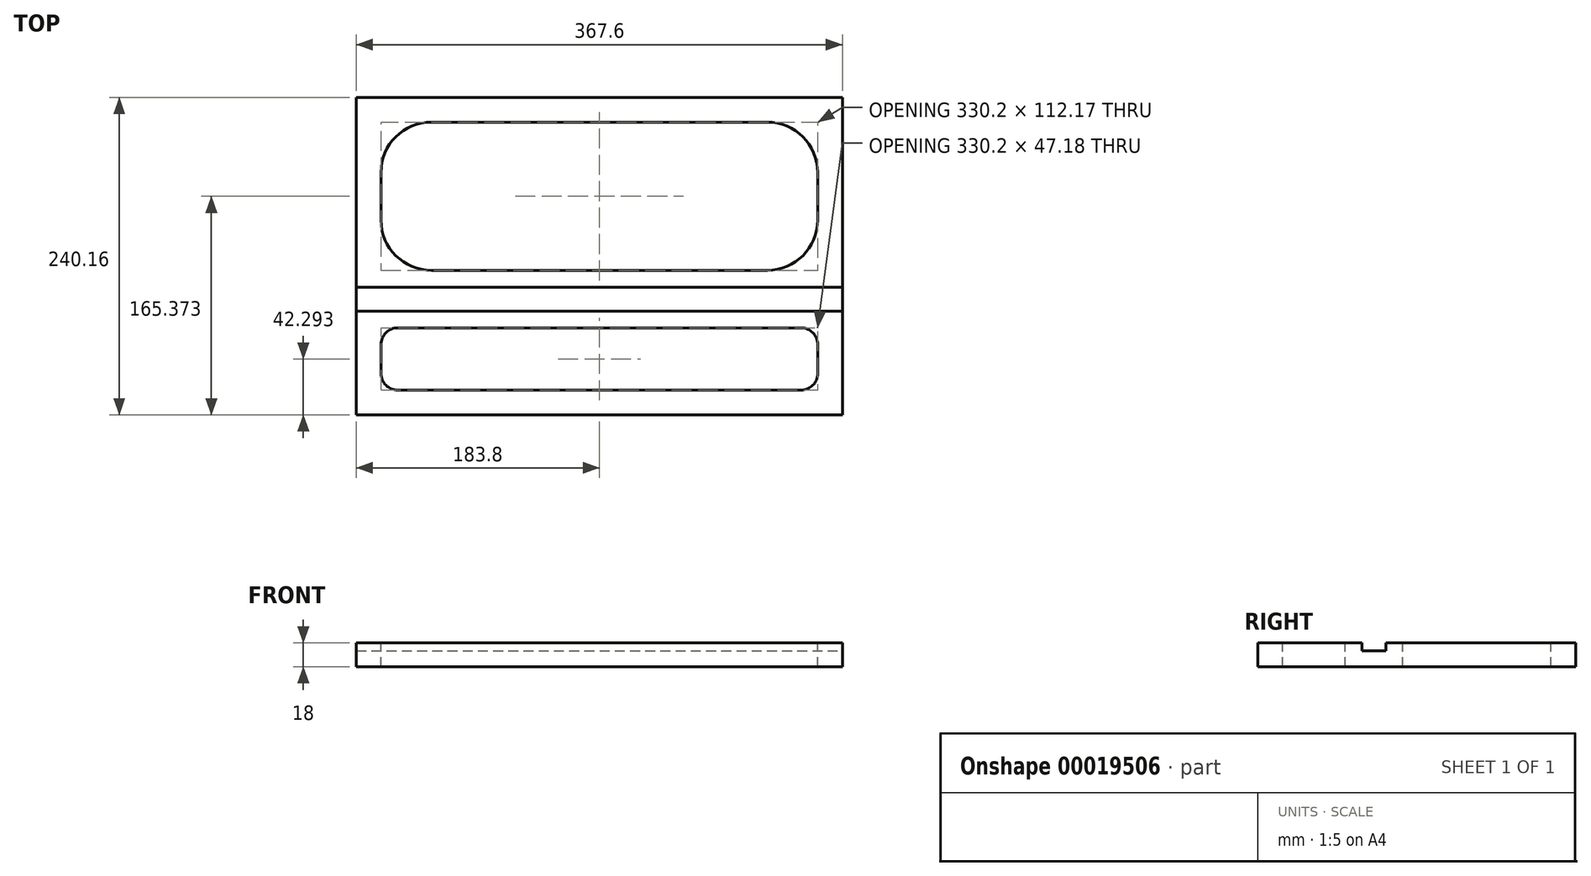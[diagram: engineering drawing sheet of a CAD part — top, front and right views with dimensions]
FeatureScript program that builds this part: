
annotation { "Feature Type Name" : "Feature", "Feature Type Description" : "" }
export const myFeature = defineFeature(function(context is Context, id is Id, definition is map)
    precondition{}
    {
        {
            var Q0;
            Q0=qCreatedBy(makeId("Top.planeOp"),FACE);
            var sketch = newSketch(context, id + "F0", { "sketchPlane" : qUnion([Q0])});
            skLineSegment(sketch, "E0.rect.bottom", {"start": v(-183.8, 120.08) * mm, "end": v(183.8, 120.08) * mm});
            skLineSegment(sketch, "E0.rect.top", {"start": v(-183.8, -120.08) * mm, "end": v(183.8, -120.08) * mm});
            skLineSegment(sketch, "E0.rect.left", {"start": v(-183.8, 120.08) * mm, "end": v(-183.8, -120.08) * mm});
            skLineSegment(sketch, "E0.rect.right", {"start": v(183.8, 120.08) * mm, "end": v(183.8, -120.08) * mm});
            skPoint(sketch, "E0.rect.middle", {"position": v(0, 0) * mm});
            skSolve(sketch);
        }
        {
            var Q0;
            Q0 = qSketchRegion(id + "F0", true);
            extrude(context, id + "F1", {"entities" : qUnion([Q0]), "depth" : 18 * mm});
        }
        {
            var Q0;
            Q0=makeQuery(id+"F1.opExtrude","CAP_FACE",FACE,{"disambiguationData":[OSD([sQuery(id+"F0.wireOp",EDGE,"E0.rect.bottom"),sQuery(id+"F0.wireOp",EDGE,"E0.rect.top"),sQuery(id+"F0.wireOp",EDGE,"E0.rect.left"),sQuery(id+"F0.wireOp",EDGE,"E0.rect.right")])],"isStart":false});
            var sketch = newSketch(context, id + "F2", { "sketchPlane" : qUnion([Q0])});
            skLineSegment(sketch, "E1.rect.bottom", {"start": v(-127, 101.38) * mm, "end": v(127, 101.38) * mm});
            skLineSegment(sketch, "E1.rect.top", {"start": v(-127, -10.8) * mm, "end": v(127, -10.8) * mm});
            skLineSegment(sketch, "E1.rect.left", {"start": v(-165.1, 63.28) * mm, "end": v(-165.1, 27.3) * mm});
            skLineSegment(sketch, "E1.rect.right", {"start": v(165.1, 63.28) * mm, "end": v(165.1, 27.3) * mm});
            skPoint(sketch, "E1.rect.middle", {"position": v(0, 45.3) * mm});
            skPoint(sketch, "E2.visualSharp", {"position": v(-165.1, 101.38) * mm});
            skArc(sketch, "E2.filletArc", {"start": v(-127, 101.38) * mm, "mid": v(-153.94, 90.22) * mm, "end": v(-165.1, 63.28) * mm});
            skPoint(sketch, "E3.visualSharp", {"position": v(165.1, 101.38) * mm});
            skArc(sketch, "E3.filletArc", {"start": v(165.1, 63.28) * mm, "mid": v(153.94, 90.22) * mm, "end": v(127, 101.38) * mm});
            skPoint(sketch, "E4.visualSharp", {"position": v(-165.1, -10.8) * mm});
            skArc(sketch, "E4.filletArc", {"start": v(-165.1, 27.3) * mm, "mid": v(-153.94, 0.37) * mm, "end": v(-127, -10.8) * mm});
            skPoint(sketch, "E5.visualSharp", {"position": v(165.1, -10.8) * mm});
            skArc(sketch, "E5.filletArc", {"start": v(127, -10.8) * mm, "mid": v(153.94, 0.37) * mm, "end": v(165.1, 27.3) * mm});
            skSolve(sketch);
        }
        {
            var Q0;
            Q0 = qSketchRegion(id + "F2", true);
            extrude(context, id + "F3", {"entities" : qUnion([Q0]), "operationType" : NewBodyOperationType.REMOVE, "oppositeDirection" : true, "depth" : 25.4 * mm});
        }
        {
            var Q0;
            Q0=makeQuery(id+"F1.opExtrude","CAP_FACE",FACE,{"disambiguationData":[OSD([sQuery(id+"F0.wireOp",EDGE,"E0.rect.bottom"),sQuery(id+"F0.wireOp",EDGE,"E0.rect.top"),sQuery(id+"F0.wireOp",EDGE,"E0.rect.left"),sQuery(id+"F0.wireOp",EDGE,"E0.rect.right")])],"isStart":false});
            var sketch = newSketch(context, id + "F4", { "sketchPlane" : qUnion([Q0])});
            skLineSegment(sketch, "E6.bottom", {"start": v(-190.85, -23.5) * mm, "end": v(190.15, -23.5) * mm});
            skLineSegment(sketch, "E6.top", {"start": v(-190.85, -41.5) * mm, "end": v(190.15, -41.5) * mm});
            skLineSegment(sketch, "E6.left", {"start": v(-190.85, -23.5) * mm, "end": v(-190.85, -41.5) * mm});
            skLineSegment(sketch, "E6.right", {"start": v(190.15, -23.5) * mm, "end": v(190.15, -41.5) * mm});
            skSolve(sketch);
        }
        {
            var Q0;
            {var subQ3=sQuery(id+"F4.wireOp",EDGE,"E6.bottom");var subQ5=makeQuery(id+"F1.opExtrude","CAP_EDGE",EDGE,{"disambiguationData":[OSD([sQuery(id+"F0.wireOp",EDGE,"E0.rect.left")])],"isStart":false});var subQ7=makeQuery(id+"F4.imprint","INTERSECT",VERTEX,{"derivedFrom":[subQ5,subQ3]});Q0=makeQuery(id+"F4.imprint","IMPRINT",FACE,{"disambiguationData":[TD([[makeQuery(id+"F4.imprint","IMPRINT",EDGE,{"disambiguationData":[TD([[subQ7,-1.0]])],"derivedFrom":subQ3}),-1.0]])]});}
            var Q1;
            {var subQ3=sQuery(id+"F4.wireOp",EDGE,"E6.bottom");var subQ5=makeQuery(id+"F1.opExtrude","CAP_EDGE",EDGE,{"disambiguationData":[OSD([sQuery(id+"F0.wireOp",EDGE,"E0.rect.right")])],"isStart":false});var subQ7=makeQuery(id+"F4.imprint","INTERSECT",VERTEX,{"derivedFrom":[subQ5,subQ3]});Q1=makeQuery(id+"F4.imprint","IMPRINT",FACE,{"disambiguationData":[TD([[makeQuery(id+"F4.imprint","IMPRINT",EDGE,{"disambiguationData":[TD([[subQ7,1.0]])],"derivedFrom":subQ3}),-1.0]])]});}
            extrude(context, id + "F5", {"entities" : qUnion([Q0, Q1]), "operationType" : NewBodyOperationType.REMOVE, "oppositeDirection" : true, "depth" : 6 * mm});
        }
        {
            var Q0;
            {var subQ0=sQuery(id+"F0.wireOp",EDGE,"E0.rect.top");var subQ1=sQuery(id+"F0.wireOp",EDGE,"E0.rect.left");var subQ2=sQuery(id+"F0.wireOp",EDGE,"E0.rect.right");Q0=makeQuery(id+"F5.boolean.opBoolean","SPLIT",FACE,{"disambiguationData":[TD([makeQuery(id+"F1.opExtrude","SWEPT_FACE",FACE,{"disambiguationData":[OSD([subQ0])]})])],"derivedFrom":makeQuery(id+"F1.opExtrude","CAP_FACE",FACE,{"disambiguationData":[OSD([sQuery(id+"F0.wireOp",EDGE,"E0.rect.bottom"),subQ0,subQ1,subQ2])],"isStart":false})});}
            var sketch = newSketch(context, id + "F6", { "sketchPlane" : qUnion([Q0])});
            skLineSegment(sketch, "E7.bottom", {"start": v(-165.1, -54.2) * mm, "end": v(165.1, -54.2) * mm});
            skLineSegment(sketch, "E7.top", {"start": v(-165.1, -101.38) * mm, "end": v(165.1, -101.38) * mm});
            skLineSegment(sketch, "E7.left", {"start": v(-165.1, -54.2) * mm, "end": v(-165.1, -101.38) * mm});
            skLineSegment(sketch, "E7.right", {"start": v(165.1, -54.2) * mm, "end": v(165.1, -101.38) * mm});
            skSolve(sketch);
        }
        {
            var Q0;
            Q0 = qSketchRegion(id + "F6", true);
            extrude(context, id + "F7", {"entities" : qUnion([Q0]), "operationType" : NewBodyOperationType.REMOVE, "oppositeDirection" : true, "depth" : 25.4 * mm});
        }
        {
            var Q0;
            Q0=makeQuery(id+"F7.boolean.opBoolean","COPY",EDGE,{"derivedFrom":makeQuery(id+"F7.opExtrude","SWEPT_EDGE",EDGE,{"disambiguationData":[OSD([sQuery(id+"F6.wireOp",EDGE,"E7.bottom"),sQuery(id+"F6.wireOp",EDGE,"E7.right")])]})});
            var Q1;
            Q1=makeQuery(id+"F7.boolean.opBoolean","COPY",EDGE,{"derivedFrom":makeQuery(id+"F7.opExtrude","SWEPT_EDGE",EDGE,{"disambiguationData":[OSD([sQuery(id+"F6.wireOp",EDGE,"E7.bottom"),sQuery(id+"F6.wireOp",EDGE,"E7.left")])]})});
            var Q2;
            Q2=makeQuery(id+"F7.boolean.opBoolean","COPY",EDGE,{"derivedFrom":makeQuery(id+"F7.opExtrude","SWEPT_EDGE",EDGE,{"disambiguationData":[OSD([sQuery(id+"F6.wireOp",EDGE,"E7.top"),sQuery(id+"F6.wireOp",EDGE,"E7.left")])]})});
            var Q3;
            Q3=makeQuery(id+"F7.boolean.opBoolean","COPY",EDGE,{"derivedFrom":makeQuery(id+"F7.opExtrude","SWEPT_EDGE",EDGE,{"disambiguationData":[OSD([sQuery(id+"F6.wireOp",EDGE,"E7.top"),sQuery(id+"F6.wireOp",EDGE,"E7.right")])]})});
            fillet(context, id + "F8", {"entities" : qUnion([Q0, Q1, Q2, Q3]), "radius" : 12.7 * mm, "tangentPropagation" : true, "allowEdgeOverflow" : false});
        }
    });
